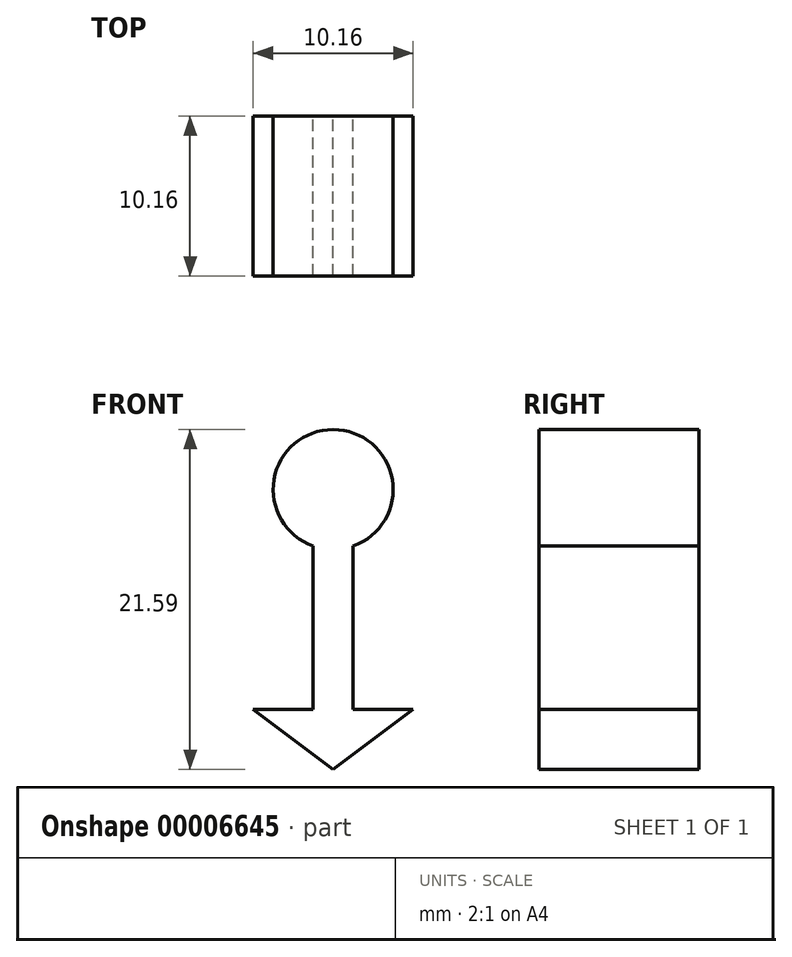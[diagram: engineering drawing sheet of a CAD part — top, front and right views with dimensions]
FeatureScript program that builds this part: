
annotation { "Feature Type Name" : "Feature", "Feature Type Description" : "" }
export const myFeature = defineFeature(function(context is Context, id is Id, definition is map)
    precondition{}
    {
        {
            var Q0;
            Q0=qCreatedBy(makeId("Front.planeOp"),FACE);
            var sketch = newSketch(context, id + "F0", { "sketchPlane" : qUnion([Q0])});
            skCircle(sketch, "E0", {"center": v(0, 0) * mm, "radius": 3.81 * mm});
            skLineSegment(sketch, "E1.bottom", {"start": v(-1.27, 0) * mm, "end": v(1.27, 0) * mm});
            skLineSegment(sketch, "E1.top", {"start": v(-1.27, -13.97) * mm, "end": v(1.27, -13.97) * mm});
            skLineSegment(sketch, "E1.left", {"start": v(-1.27, 0) * mm, "end": v(-1.27, -13.97) * mm});
            skLineSegment(sketch, "E1.right", {"start": v(1.27, 0) * mm, "end": v(1.27, -13.97) * mm});
            skLineSegment(sketch, "E2", {"start": v(-5.08, -13.97) * mm, "end": v(5.08, -13.97) * mm});
            skLineSegment(sketch, "E3", {"start": v(-5.08, -13.97) * mm, "end": v(0, -17.78) * mm});
            skLineSegment(sketch, "E4", {"start": v(0, -17.78) * mm, "end": v(5.08, -13.97) * mm});
            skSolve(sketch);
        }
        {
            var Q0;
            Q0 = qSketchRegion(id + "F0", true);
            extrude(context, id + "F1", {"entities" : qUnion([Q0]), "depth" : 10.16 * mm});
        }
    });
